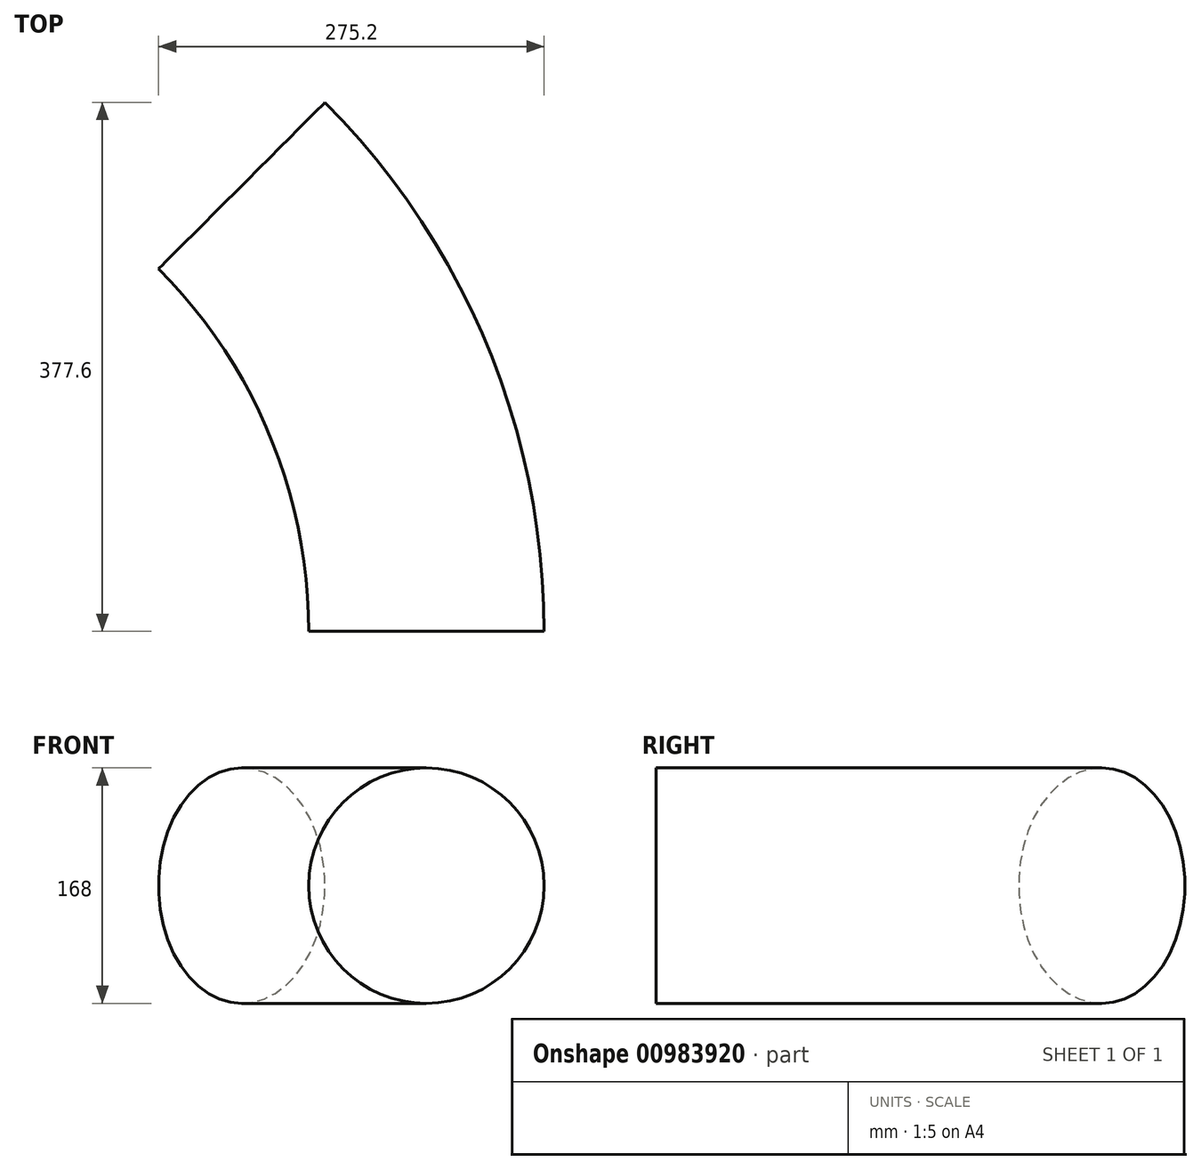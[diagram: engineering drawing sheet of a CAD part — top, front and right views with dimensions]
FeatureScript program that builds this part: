
annotation { "Feature Type Name" : "Feature", "Feature Type Description" : "" }
export const myFeature = defineFeature(function(context is Context, id is Id, definition is map)
    precondition{}
    {
        {
            var Q0;
            Q0=qCreatedBy(makeId("Top.planeOp"),FACE);
            var sketch = newSketch(context, id + "F0", { "sketchPlane" : qUnion([Q0])});
            skArc(sketch, "E0", {"start": v(450, 0) * mm, "mid": v(415.75, 172.2) * mm, "end": v(318.2, 318.2) * mm});
            skSolve(sketch);
        }
        {
            var Q0;
            Q0=qCreatedBy(makeId("Front.planeOp"),FACE);
            var sketch = newSketch(context, id + "F1", { "sketchPlane" : qUnion([Q0])});
            skCircle(sketch, "E1", {"center": v(450, 0) * mm, "radius": 84 * mm});
            skSolve(sketch);
        }
        {
            var Q0;
            Q0=makeQuery(id+"F1.imprint","IMPRINT",FACE,{"disambiguationData":[TD([[makeQuery(id+"F1.imprint","IMPRINT",EDGE,{"derivedFrom":sQuery(id+"F1.wireOp",EDGE,"E1")}),1.0]])]});
            var Q1;
            Q1=sQuery(id+"F0.wireOp",EDGE,"E0");
            sweep(context, id + "F2", {"profiles" : qUnion([Q0]), "path" : qUnion([Q1])});
        }
    });
